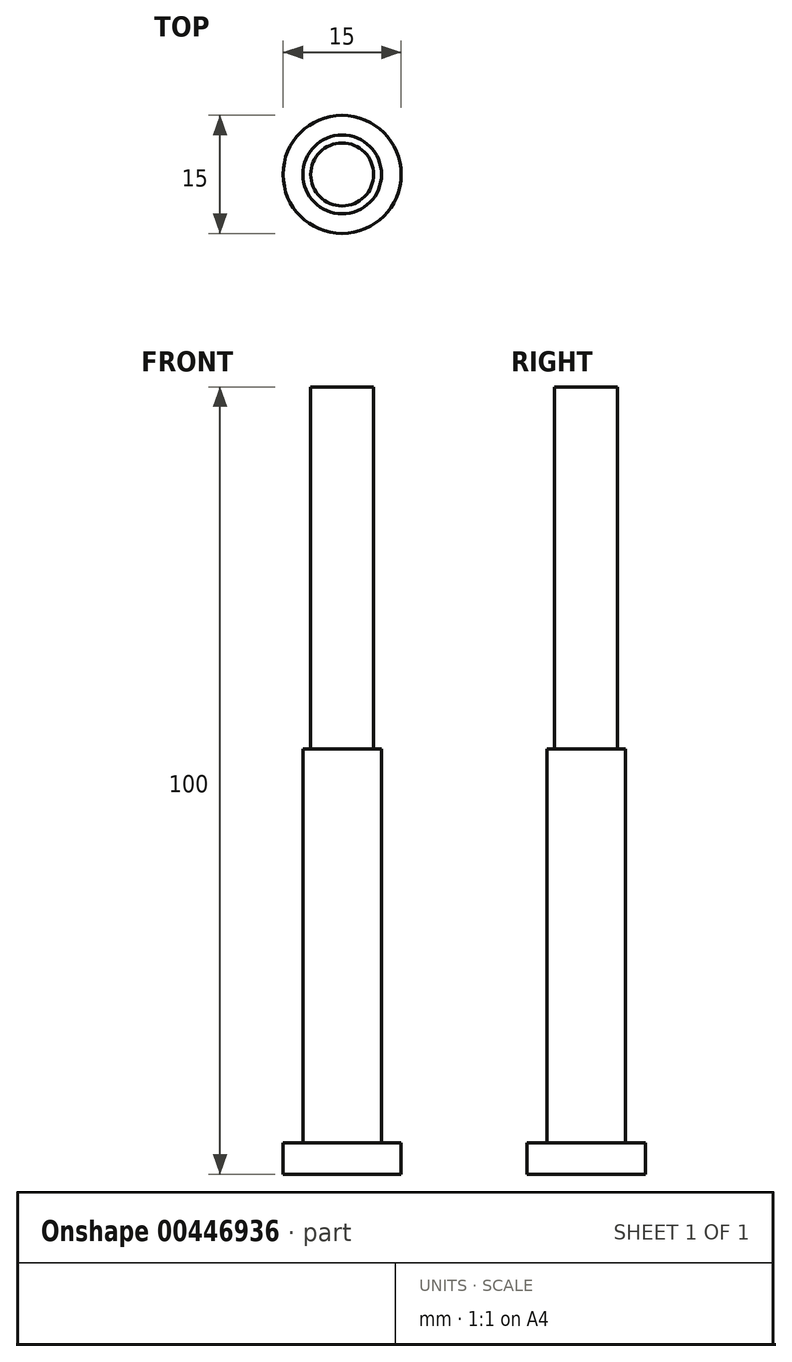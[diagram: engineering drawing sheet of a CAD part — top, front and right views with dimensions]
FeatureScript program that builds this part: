
annotation { "Feature Type Name" : "Feature", "Feature Type Description" : "" }
export const myFeature = defineFeature(function(context is Context, id is Id, definition is map)
    precondition{}
    {
        {
            var Q0;
            Q0=qCreatedBy(makeId("Top.planeOp"),FACE);
            var sketch = newSketch(context, id + "F0", { "sketchPlane" : qUnion([Q0])});
            skCircle(sketch, "E0", {"center": v(0, 0) * mm, "radius": 7.5 * mm});
            skSolve(sketch);
        }
        {
            var Q0;
            Q0=qSketchRegion(id+"F0",true);
            extrude(context, id + "F1", {"entities" : qUnion([Q0]), "depth" : 4 * mm});
        }
        {
            var Q0;
            Q0=qCreatedBy(makeId("Top.planeOp"),FACE);
            var sketch = newSketch(context, id + "F2", { "sketchPlane" : qUnion([Q0])});
            skCircle(sketch, "E1", {"center": v(0, 0) * mm, "radius": 5 * mm});
            skSolve(sketch);
        }
        {
            var Q0;
            Q0=qSketchRegion(id+"F2",true);
            extrude(context, id + "F3", {"entities" : qUnion([Q0]), "operationType" : NewBodyOperationType.ADD, "depth" : 54 * mm});
        }
        {
            var Q0;
            Q0=makeQuery(id+"F3.opExtrude","CAP_FACE",FACE,{"disambiguationData":[OSD([sQuery(id+"F2.wireOp",EDGE,"E1")])],"isStart":false});
            var sketch = newSketch(context, id + "F4", { "sketchPlane" : qUnion([Q0])});
            skCircle(sketch, "E2", {"center": v(0, 0) * mm, "radius": 4 * mm});
            skSolve(sketch);
        }
        {
            var Q0;
            Q0=makeQuery(id+"F4.imprint","IMPRINT",FACE,{"disambiguationData":[TD([[makeQuery(id+"F4.imprint","IMPRINT",EDGE,{"derivedFrom":sQuery(id+"F4.wireOp",EDGE,"E2")}),1.0]])]});
            extrude(context, id + "F5", {"entities" : qUnion([Q0]), "operationType" : NewBodyOperationType.ADD, "depth" : 46 * mm});
        }
    });
